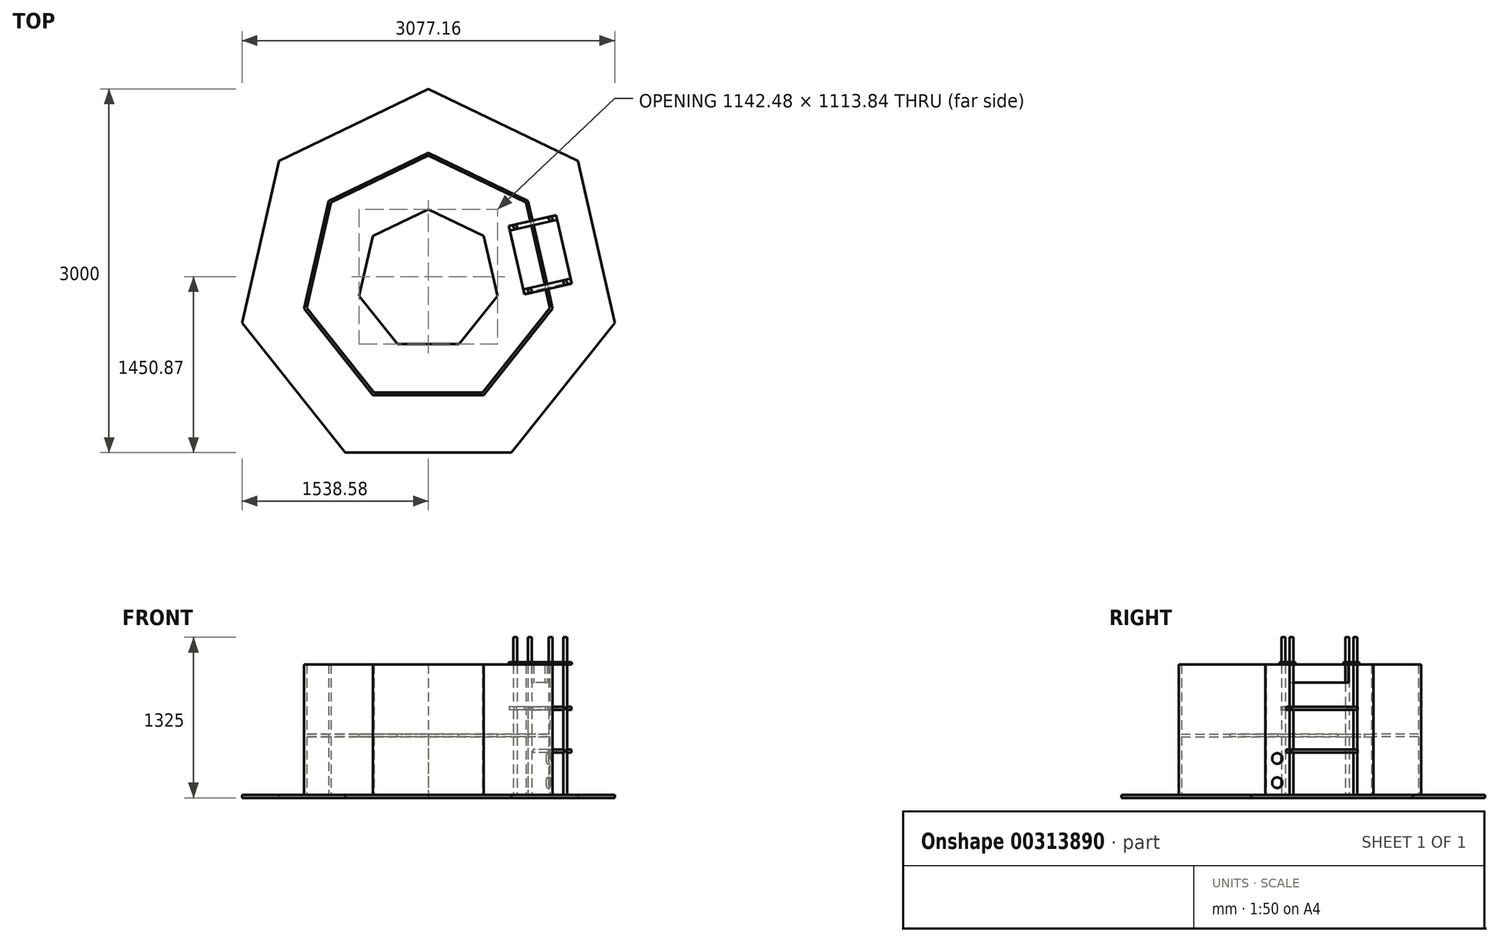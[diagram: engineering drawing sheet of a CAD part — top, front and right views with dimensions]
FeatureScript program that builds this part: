
annotation { "Feature Type Name" : "Feature", "Feature Type Description" : "" }
export const myFeature = defineFeature(function(context is Context, id is Id, definition is map)
    precondition{}
    {
        {
            var Q0;
            Q0=qCreatedBy(makeId("Top.planeOp"),FACE);
            var sketch = newSketch(context, id + "F0", { "sketchPlane" : qUnion([Q0])});
            skCircle(sketch, "E0.cCircle", {"center": v(0, 0) * mm, "radius": 1052.1 * mm, "construction": true});
            skLineSegment(sketch, "E0.0", {"start": v(0, 1052.1) * mm, "end": v(822.56, 655.97) * mm});
            skLineSegment(sketch, "E0.1", {"start": v(822.56, 655.97) * mm, "end": v(1025.72, -234.11) * mm});
            skLineSegment(sketch, "E0.2", {"start": v(1025.72, -234.11) * mm, "end": v(456.49, -947.9) * mm});
            skLineSegment(sketch, "E0.3", {"start": v(456.49, -947.9) * mm, "end": v(-456.49, -947.9) * mm});
            skLineSegment(sketch, "E0.4", {"start": v(-456.49, -947.9) * mm, "end": v(-1025.72, -234.11) * mm});
            skLineSegment(sketch, "E0.5", {"start": v(-1025.72, -234.11) * mm, "end": v(-822.56, 655.97) * mm});
            skLineSegment(sketch, "E0.6", {"start": v(-822.56, 655.97) * mm, "end": v(0, 1052.1) * mm});
            skLineSegment(sketch, "E1.0", {"start": v(1004.08, -229.17) * mm, "end": v(446.86, -927.9) * mm});
            skLineSegment(sketch, "E1.1", {"start": v(805.2, 642.13) * mm, "end": v(1004.08, -229.17) * mm});
            skLineSegment(sketch, "E1.2", {"start": v(-446.86, -927.9) * mm, "end": v(-1004.08, -229.17) * mm});
            skLineSegment(sketch, "E1.3", {"start": v(-1004.08, -229.17) * mm, "end": v(-805.2, 642.13) * mm});
            skLineSegment(sketch, "E1.4", {"start": v(-805.2, 642.13) * mm, "end": v(0, 1029.9) * mm});
            skLineSegment(sketch, "E1.5", {"start": v(446.86, -927.9) * mm, "end": v(-446.86, -927.9) * mm});
            skLineSegment(sketch, "E1.6", {"start": v(0, 1029.9) * mm, "end": v(805.2, 642.13) * mm});
            skSolve(sketch);
        }
        {
            var Q0;
            Q0=makeQuery(id+"F0.imprint","IMPRINT",FACE,{"disambiguationData":[TD([[makeQuery(id+"F0.imprint","IMPRINT",EDGE,{"derivedFrom":sQuery(id+"F0.wireOp",EDGE,"E0.0")}),-1.0]])]});
            extrude(context, id + "F1", {"entities" : qUnion([Q0]), "depth" : 1100 * mm});
        }
        {
            var Q0;
            Q0=qCreatedBy(makeId("Top.planeOp"),FACE);
            var sketch = newSketch(context, id + "F2", { "sketchPlane" : qUnion([Q0])});
            skCircle(sketch, "E2.cCircle", {"center": v(0, 0) * mm, "radius": 1578.14 * mm, "construction": true});
            skLineSegment(sketch, "E2.0", {"start": v(0, 1578.14) * mm, "end": v(1233.84, 983.96) * mm});
            skLineSegment(sketch, "E2.1", {"start": v(1233.84, 983.96) * mm, "end": v(1538.58, -351.17) * mm});
            skLineSegment(sketch, "E2.2", {"start": v(1538.58, -351.17) * mm, "end": v(684.73, -1421.86) * mm});
            skLineSegment(sketch, "E2.3", {"start": v(684.73, -1421.86) * mm, "end": v(-684.73, -1421.86) * mm});
            skLineSegment(sketch, "E2.4", {"start": v(-684.73, -1421.86) * mm, "end": v(-1538.58, -351.17) * mm});
            skLineSegment(sketch, "E2.5", {"start": v(-1538.58, -351.17) * mm, "end": v(-1233.84, 983.96) * mm});
            skLineSegment(sketch, "E2.6", {"start": v(-1233.84, 983.96) * mm, "end": v(0, 1578.14) * mm});
            skSolve(sketch);
        }
        {
            var Q0;
            Q0=makeQuery(id+"F2.imprint","IMPRINT",FACE,{"disambiguationData":[TD([[makeQuery(id+"F2.imprint","IMPRINT",EDGE,{"derivedFrom":sQuery(id+"F2.wireOp",EDGE,"E2.0")}),-1.0]])]});
            extrude(context, id + "F3", {"entities" : qUnion([Q0]), "operationType" : NewBodyOperationType.ADD, "depth" : 25 * mm});
        }
        {
            var Q0;
            Q0=makeQuery(id+"F3.boolean.opBoolean","SPLIT",FACE,{"disambiguationData":[TD([makeQuery(id+"F1.opExtrude","SWEPT_FACE",FACE,{"disambiguationData":[OSD([sQuery(id+"F0.wireOp",EDGE,"E1.0")])]})])],"derivedFrom":makeQuery(id+"F3.opExtrude","CAP_FACE",FACE,{"disambiguationData":[OSD([sQuery(id+"F2.wireOp",EDGE,"E2.0"),sQuery(id+"F2.wireOp",EDGE,"E2.1"),sQuery(id+"F2.wireOp",EDGE,"E2.2"),sQuery(id+"F2.wireOp",EDGE,"E2.3"),sQuery(id+"F2.wireOp",EDGE,"E2.4"),sQuery(id+"F2.wireOp",EDGE,"E2.5"),sQuery(id+"F2.wireOp",EDGE,"E2.6")])],"isStart":false})});
            cPlane(context, id + "F4", {"entities" : qUnion([Q0]), "cplaneType" : CPlaneType.OFFSET, "offset" : 500 * mm, "width" : 150 * mm, "height" : 150 * mm});
        }
        {
            var Q0;
            Q0=qCreatedBy(id+"F4.planeOp",FACE);
            var sketch = newSketch(context, id + "F5", { "sketchPlane" : qUnion([Q0])});
            skCircle(sketch, "E3.cCircle", {"center": v(0, 0) * mm, "radius": 585.93 * mm, "construction": true});
            skLineSegment(sketch, "E3.0", {"start": v(0, 585.93) * mm, "end": v(458.1, 365.32) * mm});
            skLineSegment(sketch, "E3.1", {"start": v(458.1, 365.32) * mm, "end": v(571.24, -130.38) * mm});
            skLineSegment(sketch, "E3.2", {"start": v(571.24, -130.38) * mm, "end": v(254.23, -527.9) * mm});
            skLineSegment(sketch, "E3.3", {"start": v(254.23, -527.9) * mm, "end": v(-254.23, -527.9) * mm});
            skLineSegment(sketch, "E3.4", {"start": v(-254.23, -527.9) * mm, "end": v(-571.24, -130.38) * mm});
            skLineSegment(sketch, "E3.5", {"start": v(-571.24, -130.38) * mm, "end": v(-458.1, 365.32) * mm});
            skLineSegment(sketch, "E3.6", {"start": v(-458.1, 365.32) * mm, "end": v(0, 585.93) * mm});
            skLineSegment(sketch, "E4.0.0", {"start": v(-805.2, 642.13) * mm, "end": v(-1004.08, -229.17) * mm});
            skLineSegment(sketch, "E4.0.1", {"start": v(-1004.08, -229.17) * mm, "end": v(-446.86, -927.9) * mm});
            skLineSegment(sketch, "E4.0.2", {"start": v(-446.86, -927.9) * mm, "end": v(446.86, -927.9) * mm});
            skLineSegment(sketch, "E4.0.3", {"start": v(446.86, -927.9) * mm, "end": v(1004.08, -229.17) * mm});
            skLineSegment(sketch, "E4.0.4", {"start": v(1004.08, -229.17) * mm, "end": v(805.2, 642.13) * mm});
            skLineSegment(sketch, "E4.0.5", {"start": v(805.2, 642.13) * mm, "end": v(0, 1029.9) * mm});
            skLineSegment(sketch, "E4.0.6", {"start": v(0, 1029.9) * mm, "end": v(-805.2, 642.13) * mm});
            skSolve(sketch);
        }
        {
            var Q0;
            Q0=makeQuery(id+"F5.imprint","IMPRINT",FACE,{"disambiguationData":[TD([[makeQuery(id+"F5.imprint","IMPRINT",EDGE,{"derivedFrom":sQuery(id+"F5.wireOp",EDGE,"E3.0")}),1.0]])]});
            extrude(context, id + "F6", {"entities" : qUnion([Q0]), "operationType" : NewBodyOperationType.ADD, "oppositeDirection" : true, "depth" : 20 * mm});
        }
        {
            var Q0;
            Q0=makeQuery(id+"F1.opExtrude","SWEPT_FACE",FACE,{"disambiguationData":[OSD([sQuery(id+"F0.wireOp",EDGE,"E0.1")])]});
            var sketch = newSketch(context, id + "F7", { "sketchPlane" : qUnion([Q0])});
            skLineSegment(sketch, "E5.bottom", {"start": v(-250, 1100) * mm, "end": v(250, 1100) * mm});
            skLineSegment(sketch, "E5.top", {"start": v(-250, 950) * mm, "end": v(250, 950) * mm});
            skLineSegment(sketch, "E5.left", {"start": v(-250, 1100) * mm, "end": v(-250, 950) * mm});
            skLineSegment(sketch, "E5.right", {"start": v(250, 1100) * mm, "end": v(250, 950) * mm});
            skCircle(sketch, "E6", {"center": v(-356.49, 325) * mm, "radius": 44 * mm});
            skCircle(sketch, "E7", {"center": v(-356.49, 125) * mm, "radius": 44 * mm});
            skLineSegment(sketch, "E8.bottom", {"start": v(-280, 400) * mm, "end": v(280, 400) * mm});
            skLineSegment(sketch, "E8.top", {"start": v(-280, 375) * mm, "end": v(280, 375) * mm});
            skLineSegment(sketch, "E8.left", {"start": v(-280, 400) * mm, "end": v(-280, 375) * mm});
            skLineSegment(sketch, "E8.right", {"start": v(280, 400) * mm, "end": v(280, 375) * mm});
            skLineSegment(sketch, "E9.0.0", {"start": v(-1025.72, 25) * mm, "end": v(-456.49, 25) * mm});
            skLineSegment(sketch, "E9.0.1", {"start": v(-456.49, 25) * mm, "end": v(-456.49, 1100) * mm});
            skLineSegment(sketch, "E9.0.2", {"start": v(-456.49, 1100) * mm, "end": v(-1025.72, 1100) * mm});
            skLineSegment(sketch, "E9.0.3", {"start": v(-1025.72, 1100) * mm, "end": v(-1025.72, 25) * mm});
            skLineSegment(sketch, "E10.bottom", {"start": v(-280, 750) * mm, "end": v(280, 750) * mm});
            skLineSegment(sketch, "E10.top", {"start": v(-280, 725) * mm, "end": v(280, 725) * mm});
            skLineSegment(sketch, "E10.left", {"start": v(-280, 750) * mm, "end": v(-280, 725) * mm});
            skLineSegment(sketch, "E10.right", {"start": v(280, 750) * mm, "end": v(280, 725) * mm});
            skLineSegment(sketch, "E11.bottom", {"start": v(250, 1100) * mm, "end": v(290, 1100) * mm});
            skLineSegment(sketch, "E11.top", {"start": v(250, 1120) * mm, "end": v(290, 1120) * mm});
            skLineSegment(sketch, "E11.left", {"start": v(250, 1100) * mm, "end": v(250, 1120) * mm});
            skLineSegment(sketch, "E11.right", {"start": v(290, 1100) * mm, "end": v(290, 1120) * mm});
            skLineSegment(sketch, "E12.bottom", {"start": v(-250, 1100) * mm, "end": v(-290, 1100) * mm});
            skLineSegment(sketch, "E12.top", {"start": v(-250, 1120) * mm, "end": v(-290, 1120) * mm});
            skLineSegment(sketch, "E12.left", {"start": v(-250, 1100) * mm, "end": v(-250, 1120) * mm});
            skLineSegment(sketch, "E12.right", {"start": v(-290, 1100) * mm, "end": v(-290, 1120) * mm});
            skSolve(sketch);
        }
        {
            var Q0;
            Q0=makeQuery(id+"F7.imprint","IMPRINT",FACE,{"disambiguationData":[TD([[makeQuery(id+"F7.imprint","IMPRINT",EDGE,{"derivedFrom":sQuery(id+"F7.wireOp",EDGE,"E5.bottom")}),1.0]])]});
            extrude(context, id + "F8", {"entities" : qUnion([Q0]), "operationType" : NewBodyOperationType.REMOVE, "oppositeDirection" : true, "depth" : 20 * mm});
        }
        {
            var Q0;
            Q0=makeQuery(id+"F7.imprint","IMPRINT",FACE,{"disambiguationData":[TD([[makeQuery(id+"F7.imprint","IMPRINT",EDGE,{"derivedFrom":sQuery(id+"F7.wireOp",EDGE,"E6")}),1.0]])]});
            var Q1;
            Q1=makeQuery(id+"F7.imprint","IMPRINT",FACE,{"disambiguationData":[TD([[makeQuery(id+"F7.imprint","IMPRINT",EDGE,{"derivedFrom":sQuery(id+"F7.wireOp",EDGE,"E7")}),1.0]])]});
            extrude(context, id + "F9", {"entities" : qUnion([Q0, Q1]), "operationType" : NewBodyOperationType.REMOVE, "oppositeDirection" : true, "depth" : 20 * mm});
        }
        {
            var Q0;
            {var subQ0=sQuery(id+"F2.wireOp",EDGE,"E2.0");var subQ1=sQuery(id+"F2.wireOp",EDGE,"E2.2");var subQ2=sQuery(id+"F2.wireOp",EDGE,"E2.1");var subQ3=sQuery(id+"F2.wireOp",EDGE,"E2.3");var subQ4=sQuery(id+"F2.wireOp",EDGE,"E2.4");var subQ5=sQuery(id+"F2.wireOp",EDGE,"E2.5");var subQ6=sQuery(id+"F2.wireOp",EDGE,"E2.6");Q0=makeQuery(id+"F3.boolean.opBoolean","SPLIT",FACE,{"disambiguationData":[TD([makeQuery(id+"F1.opExtrude","SWEPT_FACE",FACE,{"disambiguationData":[OSD([sQuery(id+"F0.wireOp",EDGE,"E0.0")])]})])],"derivedFrom":makeQuery(id+"F3.opExtrude","CAP_FACE",FACE,{"disambiguationData":[OSD([subQ0,subQ2,subQ1,subQ3,subQ4,subQ5,subQ6])],"isStart":false})});}
            var sketch = newSketch(context, id + "F10", { "sketchPlane" : qUnion([Q0])});
            skCircle(sketch, "E13", {"center": v(1130.46, -18.92) * mm, "radius": 15 * mm});
            skCircle(sketch, "E14", {"center": v(1009, 507.24) * mm, "radius": 15 * mm});
            skCircle(sketch, "E15", {"center": v(717.82, 440.78) * mm, "radius": 15 * mm});
            skCircle(sketch, "E16", {"center": v(837.98, -85.68) * mm, "radius": 15 * mm});
            skSolve(sketch);
        }
        {
            var Q0;
            Q0=makeQuery(id+"F10.imprint","IMPRINT",FACE,{"disambiguationData":[TD([[makeQuery(id+"F10.imprint","IMPRINT",EDGE,{"derivedFrom":sQuery(id+"F10.wireOp",EDGE,"E13")}),1.0]])]});
            var Q1;
            Q1=makeQuery(id+"F10.imprint","IMPRINT",FACE,{"disambiguationData":[TD([[makeQuery(id+"F10.imprint","IMPRINT",EDGE,{"derivedFrom":sQuery(id+"F10.wireOp",EDGE,"E14")}),1.0]])]});
            var Q2;
            Q2=makeQuery(id+"F10.imprint","IMPRINT",FACE,{"disambiguationData":[TD([[makeQuery(id+"F10.imprint","IMPRINT",EDGE,{"derivedFrom":sQuery(id+"F10.wireOp",EDGE,"E15")}),1.0]])]});
            var Q3;
            Q3=makeQuery(id+"F10.imprint","IMPRINT",FACE,{"disambiguationData":[TD([[makeQuery(id+"F10.imprint","IMPRINT",EDGE,{"derivedFrom":sQuery(id+"F10.wireOp",EDGE,"E16")}),1.0]])]});
            extrude(context, id + "F11", {"entities" : qUnion([Q0, Q1, Q2, Q3]), "operationType" : NewBodyOperationType.ADD, "depth" : 1300 * mm});
        }
        {
            var Q0;
            Q0=makeQuery(id+"F7.imprint","IMPRINT",FACE,{"disambiguationData":[TD([[makeQuery(id+"F7.imprint","IMPRINT",EDGE,{"derivedFrom":sQuery(id+"F7.wireOp",EDGE,"E8.bottom")}),-1.0]])]});
            extrude(context, id + "F12", {"entities" : qUnion([Q0]), "operationType" : NewBodyOperationType.ADD, "depth" : 200 * mm});
        }
        {
            var Q0;
            Q0=makeQuery(id+"F7.imprint","IMPRINT",FACE,{"disambiguationData":[TD([[makeQuery(id+"F7.imprint","IMPRINT",EDGE,{"derivedFrom":sQuery(id+"F7.wireOp",EDGE,"E10.bottom")}),-1.0]])]});
            extrude(context, id + "F13", {"entities" : qUnion([Q0]), "operationType" : NewBodyOperationType.ADD, "endBound" : BoundingType.SYMMETRIC, "depth" : 400 * mm});
        }
        {
            var Q0;
            Q0=makeQuery(id+"F7.imprint","IMPRINT",FACE,{"disambiguationData":[TD([[makeQuery(id+"F7.imprint","IMPRINT",EDGE,{"derivedFrom":sQuery(id+"F7.wireOp",EDGE,"E11.bottom")}),-1.0]])]});
            var Q1;
            Q1=makeQuery(id+"F7.imprint","IMPRINT",FACE,{"disambiguationData":[TD([[makeQuery(id+"F7.imprint","IMPRINT",EDGE,{"derivedFrom":sQuery(id+"F7.wireOp",EDGE,"E12.bottom")}),-1.0]])]});
            extrude(context, id + "F14", {"entities" : qUnion([Q0, Q1]), "operationType" : NewBodyOperationType.ADD, "endBound" : BoundingType.SYMMETRIC, "depth" : 400 * mm});
        }
    });
